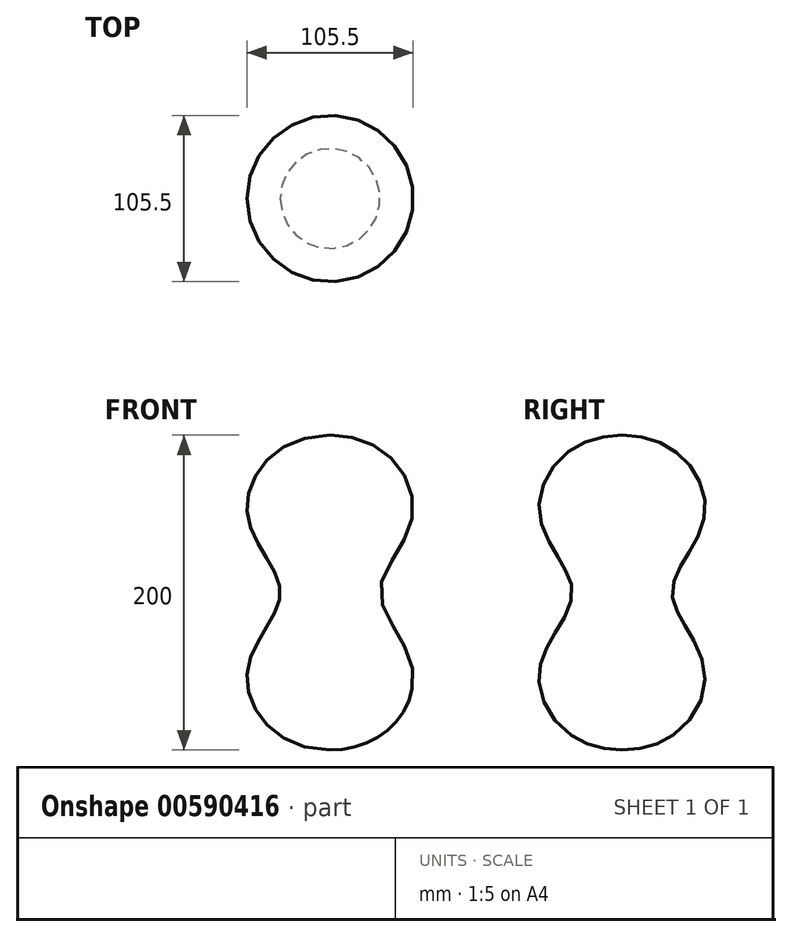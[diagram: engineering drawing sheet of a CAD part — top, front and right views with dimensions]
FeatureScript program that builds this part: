
annotation { "Feature Type Name" : "Feature", "Feature Type Description" : "" }
export const myFeature = defineFeature(function(context is Context, id is Id, definition is map)
    precondition{}
    {
        {
            var Q0;
            Q0=qCreatedBy(makeId("Front.planeOp"),FACE);
            var sketch = newSketch(context, id + "F0", { "sketchPlane" : qUnion([Q0])});
            skLineSegment(sketch, "E0", {"start": v(0, 0) * mm, "end": v(0, -100) * mm});
            skFitSpline(sketch, "E1", {"points": [v(0, -100) * mm, v(-52.51, -50) * mm, v(-31.69, 0) * mm, v(-52.51, 50) * mm, v(0, 100) * mm], "startDerivative": vector(-402.76, 0) * mm, "endDerivative": vector(402.76, 0) * mm});
            skLineSegment(sketch, "E2", {"start": v(0, 0) * mm, "end": v(0, 100) * mm});
            skSolve(sketch);
        }
        {
            var Q0;
            Q0 = qSketchRegion(id + "F0", true);
            var Q1;
            Q1=sQuery(id+"F0.wireOp",EDGE,"E2");
            revolve(context, id + "F1", {"entities" : qUnion([Q0]), "axis" : qUnion([Q1]), "revolveType" : RevolveType.FULL});
        }
    });
